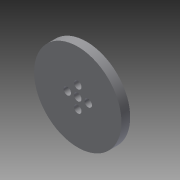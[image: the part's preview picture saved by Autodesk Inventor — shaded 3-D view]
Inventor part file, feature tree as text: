
AUTODESK INVENTOR PART (.ipt)
format: ipt  version: 2015 (Build 190159000, 159)  size: 112,640 bytes
history: native  units: mm
features: sketch x6, extrude x5, pattern_circular x1
ambient origin geometry x8: Origin, YZ Plane, XZ Plane, XY Plane, X Axis, Y Axis, Z Axis, Center Point
bodies: Solid1 (feature_tree)
feature tree (12):
  extrude  "Extrusion1"  Depth=8.0mm
  extrude  "Extrusion2"  Depth=5.0mm TaperAngle=0.0deg
  extrude  "Extrusion3"  Depth=7.8mm
  extrude  "Extrusion4"  Depth=9.0mm
  pattern_circular  "Circular Pattern1"  [2 undecoded]
  extrude  "Extrusion5"  Depth=1.0mm TaperAngle=0.0deg
  sketch  "Sketch7"  dims[d12=6.0mm d13=4.25mm d14=1.0mm d15=0.0mm d16=40.0mm d17=360.0deg d19=18.0mm d20=4.25mm d21=1.0mm d22=0.0mm]
  sketch  "Sketch1"  dims[d0=19.05mm d1=8.0mm]
  sketch  "Sketch2"  dims[d2=50.0mm d3=5.0mm d4=0.0mm]
  sketch  "Sketch4"  dims[d5=19.05mm d6=7.8mm]
  sketch  "Sketch5"  dims[d7=9.0mm d8=0.0mm d9=18.5mm]
  sketch  "Sketch6"  dims[d10=2.0mm d11=0.0mm]
note: 2 required parameter values undecoded (feature->parameter linkage not recoverable at this tier; creation-order binding heuristic only, values carry confidence <= 0.55)
